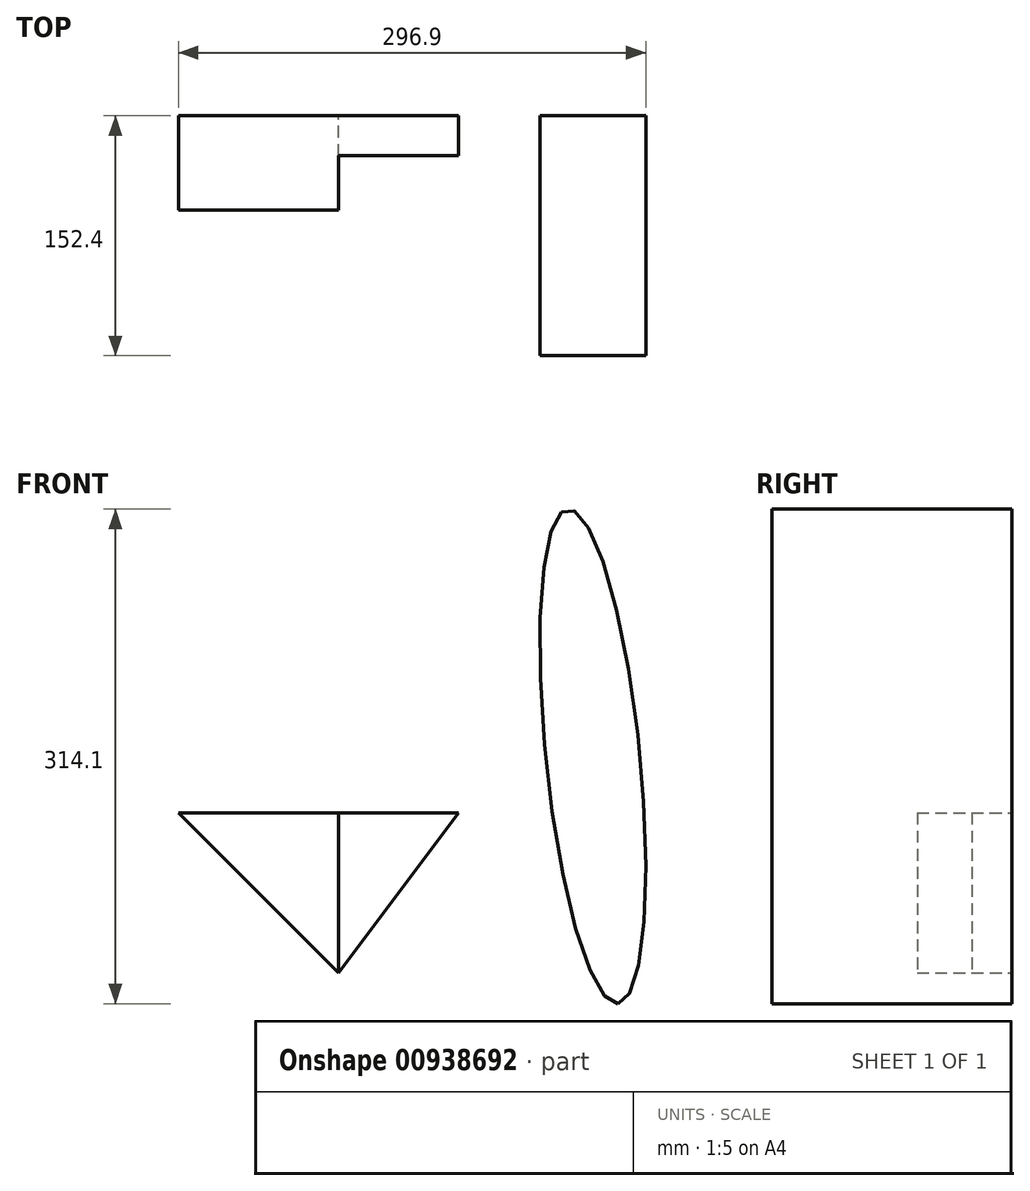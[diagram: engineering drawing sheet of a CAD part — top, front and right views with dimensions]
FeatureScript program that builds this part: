
annotation { "Feature Type Name" : "Feature", "Feature Type Description" : "" }
export const myFeature = defineFeature(function(context is Context, id is Id, definition is map)
    precondition{}
    {
        {
            var Q0;
            Q0=qCreatedBy(makeId("Front.planeOp"),FACE);
            var sketch = newSketch(context, id + "F0", { "sketchPlane" : qUnion([Q0])});
            skLineSegment(sketch, "E0", {"start": v(-101.6, 0) * mm, "end": v(0, 0) * mm});
            skLineSegment(sketch, "E1", {"start": v(-101.6, 0) * mm, "end": v(0, -101.6) * mm});
            skLineSegment(sketch, "E2", {"start": v(0, 0) * mm, "end": v(0, -101.6) * mm});
            skLineSegment(sketch, "E3", {"start": v(0, 0) * mm, "end": v(76.2, 0) * mm});
            skLineSegment(sketch, "E4", {"start": v(76.2, 0) * mm, "end": v(0, -101.6) * mm});
            skSolve(sketch);
        }
        {
            var Q0;
            Q0 = qSketchRegion(id + "F0", true);
            var sketch = newSketch(context, id + "F1", { "sketchPlane" : qUnion([Q0])});
            skSolve(sketch);
        }
        {
            var Q0;
            Q0=makeQuery(id+"F0.imprint","IMPRINT",FACE,{"disambiguationData":[TD([[makeQuery(id+"F0.imprint","IMPRINT",EDGE,{"derivedFrom":sQuery(id+"F0.wireOp",EDGE,"E2")}),1.0]])]});
            extrude(context, id + "F2", {"entities" : qUnion([Q0]), "depth" : 25.4 * mm, "offsetDistance" : 25.4 * mm});
        }
        {
            var Q0;
            Q0=makeQuery(id+"F1.imprint","IMPRINT",FACE,{"disambiguationData":[TD([[makeQuery(id+"F1.imprint","IMPRINT",EDGE,{"derivedFrom":makeQuery(id+"F0.imprint","IMPRINT",EDGE,{"derivedFrom":sQuery(id+"F0.wireOp",EDGE,"E0")})}),-1.0]])]});
            extrude(context, id + "F3", {"entities" : qUnion([Q0]), "operationType" : NewBodyOperationType.ADD, "depth" : 60.1 * mm, "offsetDistance" : 25.4 * mm});
        }
        {
            var Q0;
            Q0=qCreatedBy(makeId("Front.planeOp"),FACE);
            var sketch = newSketch(context, id + "F4", { "sketchPlane" : qUnion([Q0])});
            skEllipse(sketch, "E5", {"center": v(161.6, 35.75) * mm, "majorRadius": 157.83 * mm, "minorRadius": 29.86 * mm, "majorAxis": v(0.1, -1)});
            skSolve(sketch);
        }
        {
            var Q0;
            Q0 = qSketchRegion(id + "F4", true);
            extrude(context, id + "F5", {"entities" : qUnion([Q0]), "depth" : 152.4 * mm, "offsetDistance" : 25.4 * mm});
        }
    });
